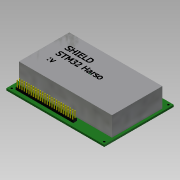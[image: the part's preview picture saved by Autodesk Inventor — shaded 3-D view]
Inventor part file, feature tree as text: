
AUTODESK INVENTOR PART (.ipt)
format: ipt  version: 2015 SP1 (Build 190203100, 203)  size: 1,303,040 bytes
history: native  units: mm
features: extrude x6, sketch x5, projected_geometry x2, pattern_linear x1, mirror x1
ambient origin geometry x8: Origin, YZ Plane, XZ Plane, XY Plane, X Axis, Y Axis, Z Axis, Center Point
bodies: Body1 (feature_tree)
feature tree (15):
  sketch  "Sketch1"  dims[d0=107.193mm d1=75.991mm]
  extrude  "Extrusion2"  Depth=75.991mm
  extrude  "Extrusion3"  Depth=2.0mm
  pattern_linear  "Rectangular Pattern1"  Spacing1=3.0mm  [1 undecoded]
  extrude  "Extrusion4"  Depth=21.26mm
  mirror  "Mirror1"
  extrude  "Extrusion5"  Depth=21.26mm
  extrude  "Extrusion6"  Depth=21.26mm
  extrude  "Extrusion7"  Depth=21.26mm
  sketch  "Sketch5"  dims[d6=3.0mm d7=3.0mm d8=3.0mm d9=3.0mm d10=3.0mm d11=3.0mm d12=3.0mm d13=3.0mm d16=0.793mm d17=0.784mm d18=4.808mm d19=1.455mm d20=250.0mm d22=2.52mm d23=20.0mm d25=2.5mm d28=0.784mm d29=4.415mm d30=250.0mm d32=2.52mm d33=20.0mm d35=2.5mm d38=1.27mm d39=1.27mm d40=1.27mm d41=1.27mm d42=2.0mm d43=0.0mm d44=11.5mm d45=0.0mm d46=250.0mm d48=2.52mm d49=20.0mm d51=2.5mm d52=7.0mm d53=0.0mm d54=2.0mm d55=0.0mm d56=63.0mm d57=4.0mm d58=0.836mm d59=0.358mm d61=2.5mm d62=0.0mm d65=21.26mm d66=0.0mm]
  sketch  "Sketch2"  dims[d2=2.0mm d3=2.0mm]
  sketch  "Sketch3"  dims[d4=2.0mm]
  projected_geometry  "Projected Loop1"
  projected_geometry  "Projected Loop2"
  sketch  "Sketch4"  dims[d5=2.0mm]
note: 1 required parameter value undecoded (feature->parameter linkage not recoverable at this tier; creation-order binding heuristic only, values carry confidence <= 0.55)
